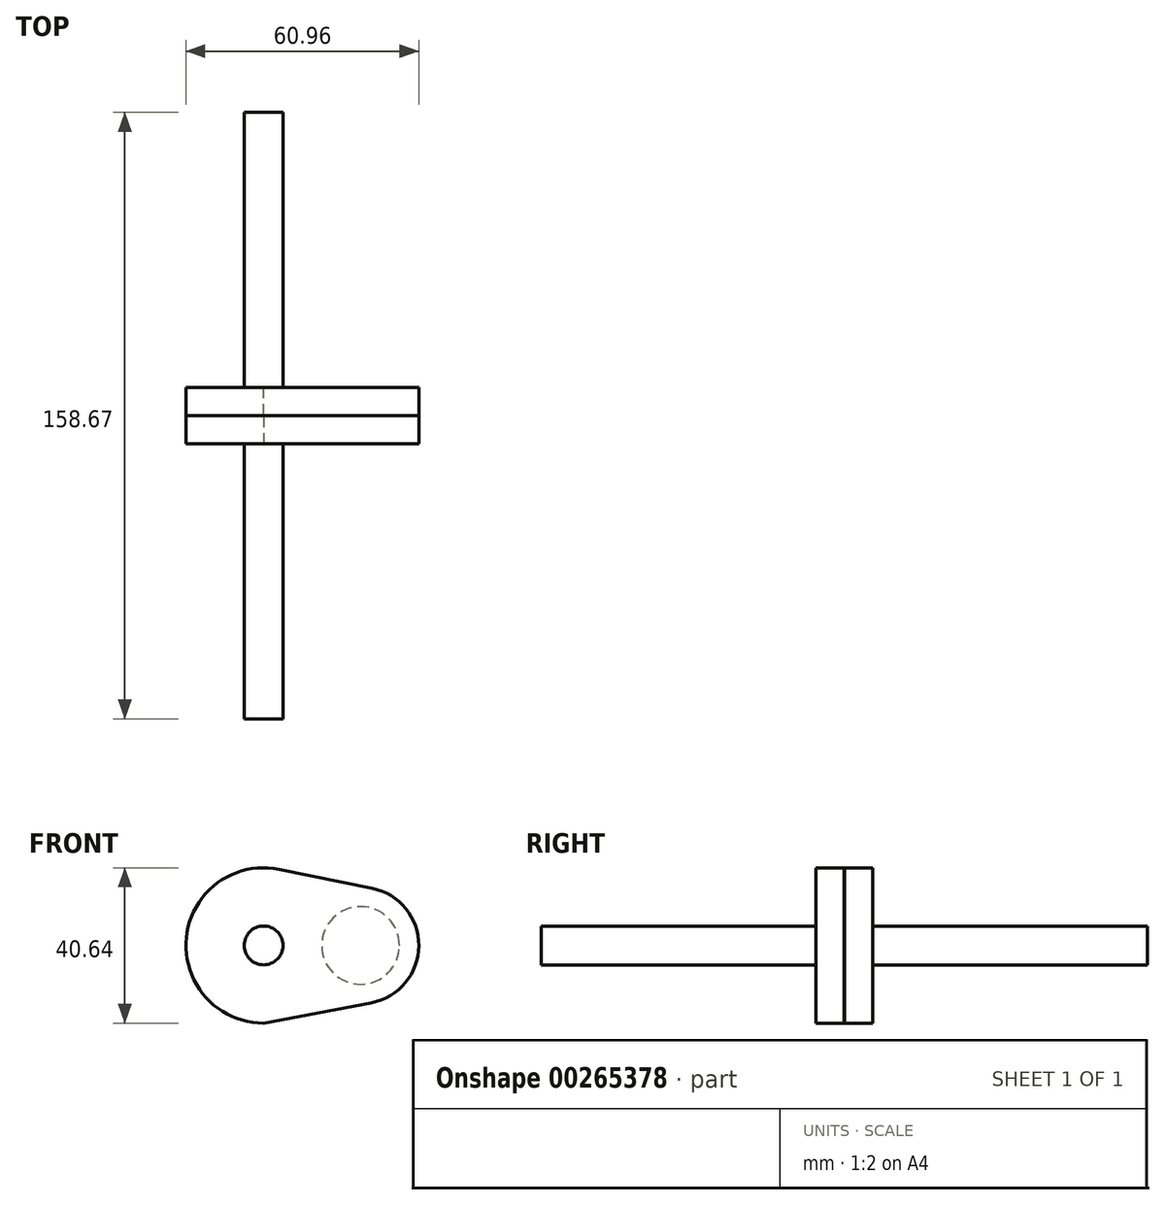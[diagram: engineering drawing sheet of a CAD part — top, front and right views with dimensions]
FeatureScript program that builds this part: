
annotation { "Feature Type Name" : "Feature", "Feature Type Description" : "" }
export const myFeature = defineFeature(function(context is Context, id is Id, definition is map)
    precondition{}
    {
        {
            var Q0;
            Q0=qCreatedBy(makeId("Front.planeOp"),FACE);
            var sketch = newSketch(context, id + "F0", { "sketchPlane" : qUnion([Q0])});
            skArc(sketch, "E0", {"start": v(4.06, 19.9) * mm, "mid": v(-20.24, -1.75) * mm, "end": v(7.43, -18.91) * mm});
            skCircle(sketch, "E1", {"center": v(0, 0) * mm, "radius": 5.08 * mm});
            skCircle(sketch, "E2", {"center": v(25.4, 0) * mm, "radius": 10.16 * mm});
            skArc(sketch, "E3", {"start": v(28.24, -14.97) * mm, "mid": v(40.64, -0.1) * mm, "end": v(28.45, 14.93) * mm});
            skLineSegment(sketch, "E4", {"start": v(4.06, 19.9) * mm, "end": v(28.45, 14.93) * mm});
            skLineSegment(sketch, "E5", {"start": v(0, -20.32) * mm, "end": v(28.24, -14.97) * mm});
            skSolve(sketch);
        }
        {
            var Q0;
            Q0=makeQuery(id+"F0.imprint","IMPRINT",FACE,{"disambiguationData":[TD([[makeQuery(id+"F0.imprint","IMPRINT",EDGE,{"derivedFrom":sQuery(id+"F0.wireOp",EDGE,"E1")}),-1.0]])]});
            var Q1;
            Q1=makeQuery(id+"F0.imprint","IMPRINT",FACE,{"disambiguationData":[TD([[makeQuery(id+"F0.imprint","IMPRINT",EDGE,{"derivedFrom":sQuery(id+"F0.wireOp",EDGE,"E2")}),1.0]])]});
            extrude(context, id + "F1", {"entities" : qUnion([Q0, Q1]), "depth" : 7.37 * mm});
        }
        {
            var Q0;
            Q0=makeQuery(id+"F1.opExtrude","CAP_FACE",FACE,{"disambiguationData":[OSD([sQuery(id+"F0.wireOp",EDGE,"E0"),sQuery(id+"F0.wireOp",EDGE,"E1"),sQuery(id+"F0.wireOp",EDGE,"E3"),sQuery(id+"F0.wireOp",EDGE,"E4"),sQuery(id+"F0.wireOp",EDGE,"E5")])],"isStart":false});
            var sketch = newSketch(context, id + "F2", { "sketchPlane" : qUnion([Q0])});
            skCircle(sketch, "E6.0", {"center": v(25.4, 0) * mm, "radius": 10.16 * mm});
            skSolve(sketch);
        }
        {
            var Q0;
            Q0 = qSketchRegion(id + "F2", true);
            extrude(context, id + "F3", {"entities" : qUnion([Q0]), "operationType" : NewBodyOperationType.ADD, "depth" : .5511 / 50.8 * mm});
        }
        {
            var Q0;
            Q0=makeQuery(id+"F3.opExtrude","CAP_FACE",FACE,{"disambiguationData":[OSD([sQuery(id+"F2.wireOp",EDGE,"E6.0")])],"isStart":false});
            cPlane(context, id + "F4", {"entities" : qUnion([Q0]), "cplaneType" : CPlaneType.OFFSET, "offset" : 0 * mm, "width" : 152.4 * mm, "height" : 152.4 * mm});
        }
        {
            var Q0;
            Q0=makeQuery(id+"F1.opExtrude","SWEPT_BODY",BODY,{"disambiguationData":[OSD([sQuery(id+"F0.wireOp",EDGE,"E0"),sQuery(id+"F0.wireOp",EDGE,"E1"),sQuery(id+"F0.wireOp",EDGE,"E3"),sQuery(id+"F0.wireOp",EDGE,"E4"),sQuery(id+"F0.wireOp",EDGE,"E5")])]});
            var Q1;
            Q1=qCreatedBy(id+"F4.planeOp",FACE);
            mirror(context, id + "F5", {"operationType" : NewBodyOperationType.ADD, "entities" : qUnion([Q0]), "mirrorPlane" : qUnion([Q1])});
        }
        {
            var Q0;
            Q0=makeQuery(id+"F5.opPattern","COPY",FACE,{"derivedFrom":makeQuery(id+"F1.opExtrude","CAP_FACE",FACE,{"disambiguationData":[OSD([sQuery(id+"F0.wireOp",EDGE,"E0"),sQuery(id+"F0.wireOp",EDGE,"E1"),sQuery(id+"F0.wireOp",EDGE,"E3"),sQuery(id+"F0.wireOp",EDGE,"E4"),sQuery(id+"F0.wireOp",EDGE,"E5")])],"isStart":true}),"instanceName":"1"});
            cPlane(context, id + "F6", {"entities" : qUnion([Q0]), "cplaneType" : CPlaneType.OFFSET, "offset" : 7.62 * mm, "oppositeDirection" : true, "width" : 152.4 * mm, "height" : 152.4 * mm});
        }
        {
            var Q0;
            Q0=qCreatedBy(id+"F6.planeOp",FACE);
            var sketch = newSketch(context, id + "F7", { "sketchPlane" : qUnion([Q0])});
            skCircle(sketch, "E7.0", {"center": v(0, 0) * mm, "radius": 5.08 * mm});
            skSolve(sketch);
        }
        {
            var Q0;
            Q0 = qSketchRegion(id + "F7", true);
            extrude(context, id + "F8", {"entities" : qUnion([Q0]), "depth" : 79.58 * mm});
        }
        {
            var Q0;
            Q0=makeQuery(id+"F8.opExtrude","SWEPT_BODY",BODY,{"disambiguationData":[OSD([sQuery(id+"F7.wireOp",EDGE,"E7.0")])]});
            var Q1;
            Q1=qCreatedBy(id+"F4.planeOp",FACE);
            mirror(context, id + "F9", {"operationType" : NewBodyOperationType.ADD, "entities" : qUnion([Q0]), "mirrorPlane" : qUnion([Q1])});
        }
    });
